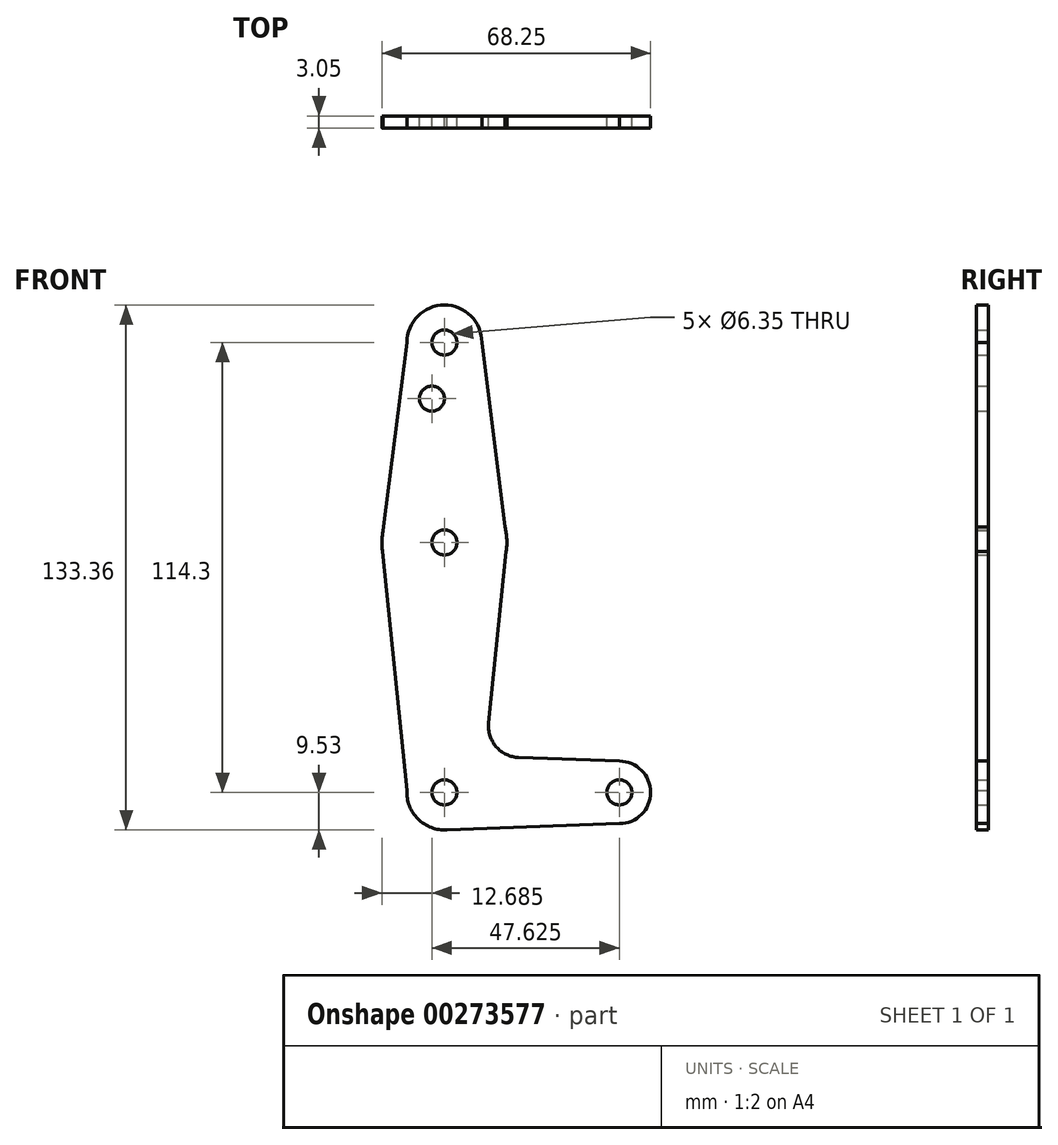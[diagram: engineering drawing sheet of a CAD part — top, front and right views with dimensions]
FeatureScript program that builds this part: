
annotation { "Feature Type Name" : "Feature", "Feature Type Description" : "" }
export const myFeature = defineFeature(function(context is Context, id is Id, definition is map)
    precondition{}
    {
        {
            var Q0;
            Q0=qCreatedBy(makeId("Front.planeOp"),FACE);
            var sketch = newSketch(context, id + "F0", { "sketchPlane" : qUnion([Q0])});
            skCircle(sketch, "E0", {"center": v(0.01, 63.5) * mm, "radius": 15.88 * mm});
            skCircle(sketch, "E1", {"center": v(0, 0) * mm, "radius": 9.53 * mm});
            skCircle(sketch, "E2", {"center": v(44.45, 0) * mm, "radius": 7.94 * mm});
            skLineSegment(sketch, "E3", {"start": v(0, 114.3) * mm, "end": v(0, 0) * mm});
            skLineSegment(sketch, "E4", {"start": v(0, 0) * mm, "end": v(44.45, 0) * mm});
            skCircle(sketch, "E5", {"center": v(0, 114.3) * mm, "radius": 9.53 * mm});
            skPoint(sketch, "E6", {"position": v(-15.84, 64.38) * mm});
            skPoint(sketch, "E7", {"position": v(-9.53, 114.3) * mm});
            skPoint(sketch, "E8", {"position": v(15.89, 63.5) * mm});
            skPoint(sketch, "E9", {"position": v(9.53, 114.3) * mm});
            skLineSegment(sketch, "E10", {"start": v(9.53, 114.3) * mm, "end": v(15.89, 63.5) * mm});
            skLineSegment(sketch, "E11", {"start": v(-15.84, 64.38) * mm, "end": v(-9.52, 114.3) * mm});
            skPoint(sketch, "E12", {"position": v(-15.84, 62.62) * mm});
            skPoint(sketch, "E13", {"position": v(-9.5, 0.54) * mm});
            skPoint(sketch, "E14", {"position": v(15.86, 62.62) * mm});
            skPoint(sketch, "E15", {"position": v(9.5, 0.54) * mm});
            skLineSegment(sketch, "E16", {"start": v(-15.84, 62.62) * mm, "end": v(-9.5, 0.54) * mm});
            skLineSegment(sketch, "E17", {"start": v(11.26, 17.6) * mm, "end": v(15.86, 62.62) * mm});
            skPoint(sketch, "E18", {"position": v(0, 9.53) * mm});
            skPoint(sketch, "E19", {"position": v(44.45, 7.94) * mm});
            skLineSegment(sketch, "E20", {"start": v(18.88, 8.85) * mm, "end": v(44.45, 7.94) * mm});
            skCircle(sketch, "E21", {"center": v(-3.17, 100.03) * mm, "radius": 3.18 * mm});
            skCircle(sketch, "E22", {"center": v(0, 114.3) * mm, "radius": 3.18 * mm});
            skCircle(sketch, "E23", {"center": v(0.01, 63.5) * mm, "radius": 3.18 * mm});
            skCircle(sketch, "E24", {"center": v(0, 0) * mm, "radius": 3.18 * mm});
            skCircle(sketch, "E25", {"center": v(44.45, 0) * mm, "radius": 3.18 * mm});
            skArc(sketch, "E26.filletArc", {"start": v(11.26, 17.6) * mm, "mid": v(13.17, 11.57) * mm, "end": v(18.88, 8.85) * mm});
            skPoint(sketch, "E27", {"position": v(0, -9.53) * mm});
            skPoint(sketch, "E28", {"position": v(44.45, -7.94) * mm});
            skLineSegment(sketch, "E29", {"start": v(0, -9.52) * mm, "end": v(44.45, -7.94) * mm});
            skSolve(sketch);
        }
        {
            var Q0;
            Q0 = qSketchRegion(id + "F0", true);
            var Q1;
            {var subQ0=sQuery(id+"F0.wireOp",EDGE,"E3");var subQ1=sQuery(id+"F0.wireOp",EDGE,"E1");var subQ2=makeQuery(id+"F0.imprint","INTERSECT",VERTEX,{"derivedFrom":[subQ1,subQ0]});Q1=makeQuery(id+"F0.imprint","IMPRINT",FACE,{"disambiguationData":[TD([[makeQuery(id+"F0.imprint","IMPRINT",EDGE,{"disambiguationData":[TD([[subQ2,1.0]])],"derivedFrom":subQ1}),1.0]])]});}
            extrude(context, id + "F1", {"entities" : qUnion([Q0, Q1]), "depth" : 3.05 * mm});
        }
    });
